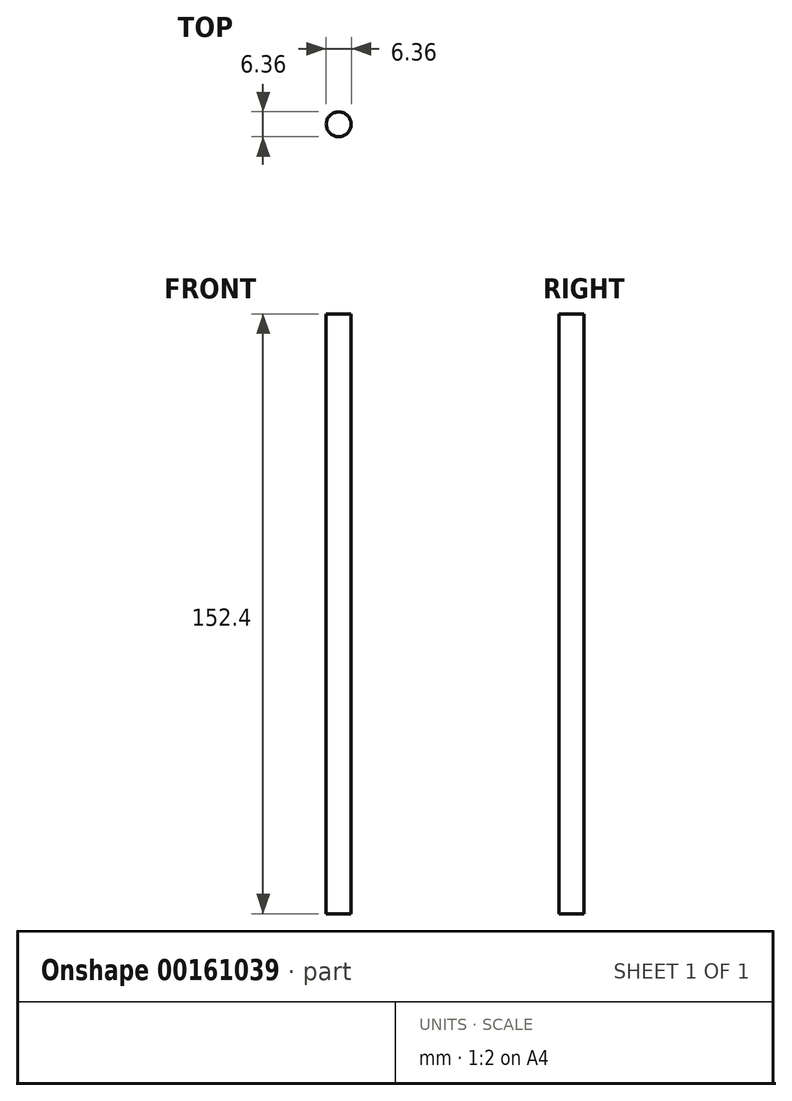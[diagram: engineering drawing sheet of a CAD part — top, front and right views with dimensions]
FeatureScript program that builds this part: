
annotation { "Feature Type Name" : "Feature", "Feature Type Description" : "" }
export const myFeature = defineFeature(function(context is Context, id is Id, definition is map)
    precondition{}
    {
        {
            var Q0;
            Q0=qCreatedBy(makeId("Top.planeOp"),FACE);
            var sketch = newSketch(context, id + "F0", { "sketchPlane" : qUnion([Q0])});
            skCircle(sketch, "E0", {"center": v(0, 0) * mm, "radius": 3.18 * mm});
            skSolve(sketch);
        }
        {
            var Q0;
            Q0 = qSketchRegion(id + "F0", true);
            extrude(context, id + "F1", {"entities" : qUnion([Q0]), "depth" : 152.4 * mm});
        }
    });
